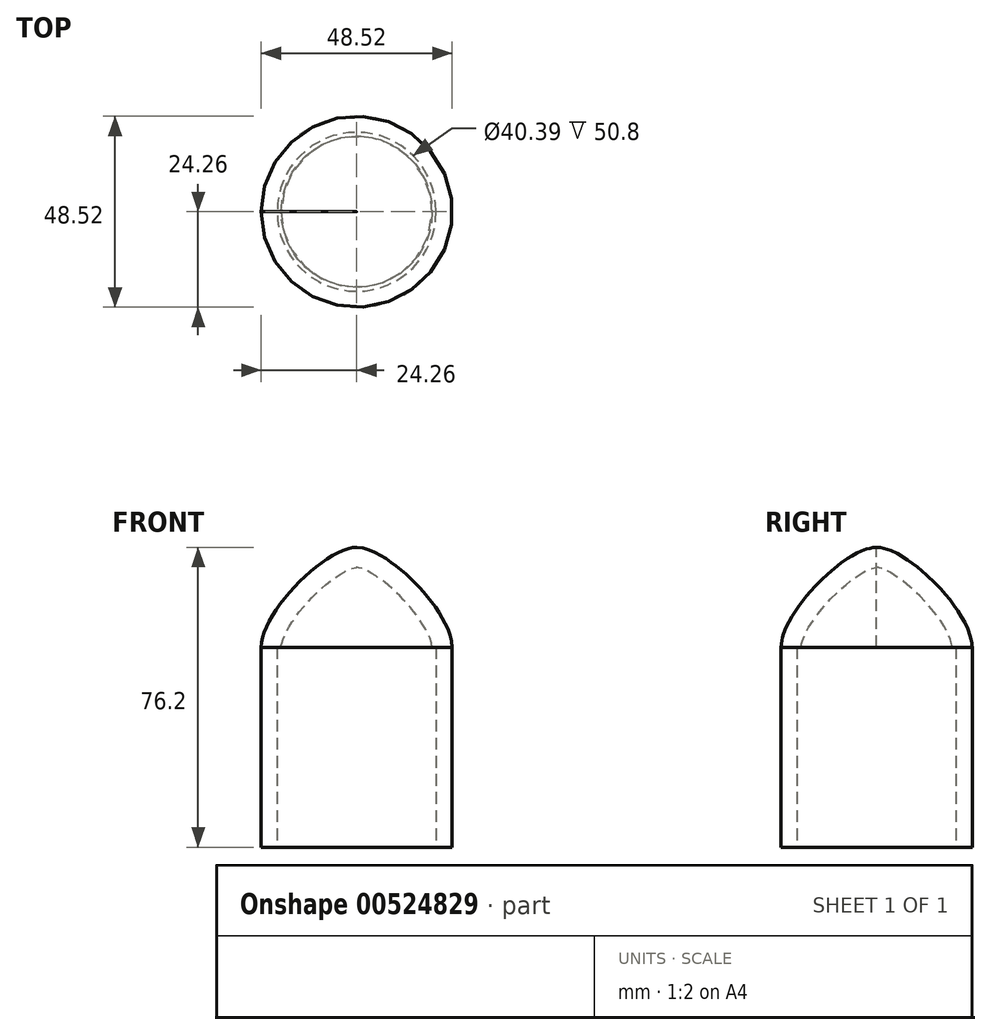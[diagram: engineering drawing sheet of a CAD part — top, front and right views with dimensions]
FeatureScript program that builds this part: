
annotation { "Feature Type Name" : "Feature", "Feature Type Description" : "" }
export const myFeature = defineFeature(function(context is Context, id is Id, definition is map)
    precondition{}
    {
        {
            var Q0;
            Q0=qCreatedBy(makeId("Top.planeOp"),FACE);
            var sketch = newSketch(context, id + "F0", { "sketchPlane" : qUnion([Q0])});
            skCircle(sketch, "E0", {"center": v(0, 0) * mm, "radius": 20.2 * mm});
            skCircle(sketch, "E1", {"center": v(0, 0) * mm, "radius": 24.26 * mm});
            skSolve(sketch);
        }
        {
            var Q0;
            Q0 = qSketchRegion(id + "F0", true);
            extrude(context, id + "F1", {"entities" : qUnion([Q0]), "depth" : 50.8 * mm, "offsetDistance" : 25.4 * mm});
        }
        {
            var Q0;
            Q0=makeQuery(id+"F1.opExtrude","CAP_FACE",FACE,{"disambiguationData":[OSD([sQuery(id+"F0.wireOp",EDGE,"E0"),sQuery(id+"F0.wireOp",EDGE,"E1")])],"isStart":false});
            var sketch = newSketch(context, id + "F2", { "sketchPlane" : qUnion([Q0])});
            skCircle(sketch, "E2.0", {"center": v(0, 0) * mm, "radius": 24.26 * mm});
            skSolve(sketch);
        }
        {
            var Q0;
            Q0=makeQuery(id+"F2.imprint","IMPRINT",FACE,{"disambiguationData":[TD([[makeQuery(id+"F2.imprint","IMPRINT",EDGE,{"derivedFrom":sQuery(id+"F2.wireOp",EDGE,"E2.0")}),1.0]])]});
            cPlane(context, id + "F3", {"entities" : qUnion([Q0]), "cplaneType" : CPlaneType.OFFSET, "offset" : 25.4 * mm, "width" : 152.4 * mm, "height" : 152.4 * mm});
        }
        {
            var Q0;
            Q0=qCreatedBy(id+"F3.planeOp",FACE);
            var sketch = newSketch(context, id + "F4", { "sketchPlane" : qUnion([Q0])});
            skPoint(sketch, "E3", {"position": v(0, 0) * mm});
            skSolve(sketch);
        }
        {
            var Q1;
            Q1 = qSketchRegion(id + "F2", true);
            var Q2;
            Q2=sQuery(id+"F4.wireOp",VERTEX,"E3");
            loft(context, id + "F5", {"operationType" : NewBodyOperationType.ADD, "startCondition" : LoftEndDerivativeType.NORMAL_TO_PROFILE, "startMagnitude" : 1, "endCondition" : LoftEndDerivativeType.TANGENT_TO_PROFILE, "endMagnitude" : 1, "sheetProfilesArray" : [{ "sheetProfileEntities" : qUnion([Q1]) }, { "sheetProfileEntities" : qUnion([Q2]) }]});
        }
        {
            var Q0;
            Q0=makeQuery(id+"F5.opLoft","CAP_FACE",FACE,{"disambiguationData":[OSD([makeQuery(id+"F2.imprint","IMPRINT",FACE,{"disambiguationData":[TD([[makeQuery(id+"F2.imprint","IMPRINT",EDGE,{"derivedFrom":makeQuery(id+"F1.opExtrude","CAP_EDGE",EDGE,{"disambiguationData":[OSD([sQuery(id+"F0.wireOp",EDGE,"E0")])],"isStart":false})}),1.0]])]})])],"isStart":true});
            shell(context, id + "F6", {"entities" : qUnion([Q0]), "thickness" : 5.08 * mm});
        }
    });
